# Revit family: Towel_Bar-DXV-Belshire-D35170180_Series
name_source: partatom
category: Specialty Equipment
units: mm (PartAtom-declared; Revit-internal decimal feet)

## family parameters
Cut with Voids When Loaded = No
Host = Face
OmniClass Number = 23.40.20.21.27
OmniClass Title = Towel Bars
Part Type = Normal
Room Calculation Point = No
Round Connector Dimension = Use Diameter
Shared = Yes

## types (4) — shared parameters
Assembly Code = C1030200
Default Elevation = 48"
Description = Belshire 18" Towel Bar
Height = 1 7/8"
Installation Instruction Link = https://dxv01.blob.core.windows.net
Installation Type = Wall Mount
Length = 3 9/16"
Manufacturer = DXV
Price = Prices may vary. Please consult Manufacturer Representative for most up-to-date price list.
Product Documentation Link = https://dxv01.blob.core.windows.net
Product Page URL = https://www.dxv.com
Revised Date = 11/12/2021
URL = https://www.dxv.com
Width = 19 1/8"

## per-type parameters (varying)
| type | Finish | Material |
| D35170180.100 | Metal-DXV-100-Polished Chrome | Metal-DXV-100-Polished Chrome |
| D35170180.144 | Metal-DXV-144-Brushed Nickel | Metal-DXV-144-Brushed Nickel |
| D35170180.150 | Metal-DXV-150-Platinum Nickel | Metal-DXV-150-Platinum Nickel |
| D35170180.427 | Metal-DXV-427-Satin Brass | Metal-DXV-427-Satin Brass |

note: column(s) folded — value = type name in every type: Model

## geometry (parser evidence)
native form markers: Sweep x2
no freeform markers — native parametric forms only
